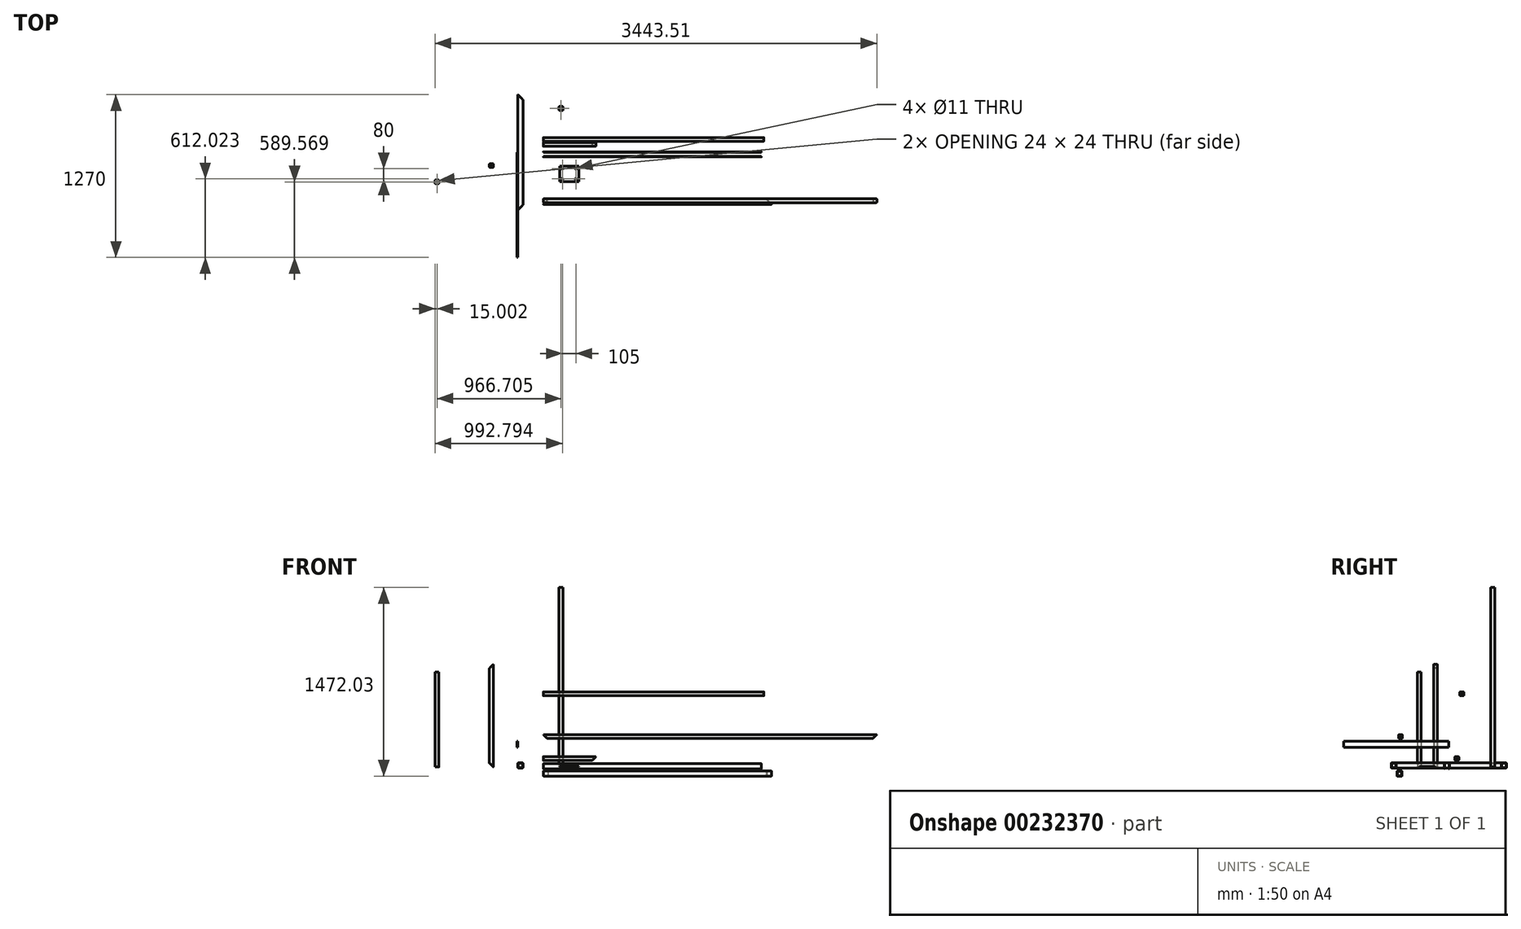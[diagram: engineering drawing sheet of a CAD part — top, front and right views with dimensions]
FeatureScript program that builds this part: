
annotation { "Feature Type Name" : "Feature", "Feature Type Description" : "" }
export const myFeature = defineFeature(function(context is Context, id is Id, definition is map)
    precondition{}
    {
        {
            var Q0;
            Q0=qCreatedBy(makeId("Right.planeOp"),FACE);
            var sketch = newSketch(context, id + "F0", { "sketchPlane" : qUnion([Q0])});
            skLineSegment(sketch, "E0.bottom", {"start": v(-31.14, 25.42) * mm, "end": v(-1.14, 25.42) * mm});
            skLineSegment(sketch, "E0.top", {"start": v(-31.14, -14.58) * mm, "end": v(-1.14, -14.58) * mm});
            skLineSegment(sketch, "E0.left", {"start": v(-36.14, 20.42) * mm, "end": v(-36.14, -9.58) * mm});
            skLineSegment(sketch, "E0.right", {"start": v(3.86, 20.42) * mm, "end": v(3.86, -9.58) * mm});
            skLineSegment(sketch, "E1.bottom", {"start": v(-31.14, 22.42) * mm, "end": v(-1.14, 22.42) * mm});
            skLineSegment(sketch, "E1.top", {"start": v(-31.14, -11.58) * mm, "end": v(-1.14, -11.58) * mm});
            skLineSegment(sketch, "E1.left", {"start": v(-33.14, 20.42) * mm, "end": v(-33.14, -9.58) * mm});
            skLineSegment(sketch, "E1.right", {"start": v(0.86, 20.42) * mm, "end": v(0.86, -9.58) * mm});
            skPoint(sketch, "E2.visualSharp", {"position": v(-36.14, 25.42) * mm});
            skArc(sketch, "E2.filletArc", {"start": v(-31.14, 25.42) * mm, "mid": v(-34.68, 23.96) * mm, "end": v(-36.14, 20.42) * mm});
            skPoint(sketch, "E3.visualSharp", {"position": v(3.86, 25.42) * mm});
            skArc(sketch, "E3.filletArc", {"start": v(3.86, 20.42) * mm, "mid": v(2.4, 23.96) * mm, "end": v(-1.14, 25.42) * mm});
            skPoint(sketch, "E4.visualSharp", {"position": v(3.86, -14.58) * mm});
            skArc(sketch, "E4.filletArc", {"start": v(-1.14, -14.58) * mm, "mid": v(2.4, -13.12) * mm, "end": v(3.86, -9.58) * mm});
            skPoint(sketch, "E5.visualSharp", {"position": v(-36.14, -14.58) * mm});
            skArc(sketch, "E5.filletArc", {"start": v(-36.14, -9.58) * mm, "mid": v(-34.68, -13.12) * mm, "end": v(-31.14, -14.58) * mm});
            skPoint(sketch, "E6.visualSharp", {"position": v(-33.14, 22.42) * mm});
            skArc(sketch, "E6.filletArc", {"start": v(-31.14, 22.42) * mm, "mid": v(-32.55, 21.83) * mm, "end": v(-33.14, 20.42) * mm});
            skPoint(sketch, "E7.visualSharp", {"position": v(0.86, 22.42) * mm});
            skArc(sketch, "E7.filletArc", {"start": v(0.86, 20.42) * mm, "mid": v(0.27, 21.83) * mm, "end": v(-1.14, 22.42) * mm});
            skPoint(sketch, "E8.visualSharp", {"position": v(0.86, -11.58) * mm});
            skArc(sketch, "E8.filletArc", {"start": v(-1.14, -11.58) * mm, "mid": v(0.27, -11) * mm, "end": v(0.86, -9.58) * mm});
            skPoint(sketch, "E9.visualSharp", {"position": v(-33.14, -11.58) * mm});
            skArc(sketch, "E9.filletArc", {"start": v(-33.14, -9.58) * mm, "mid": v(-32.55, -11) * mm, "end": v(-31.14, -11.58) * mm});
            skSolve(sketch);
        }
        {
            var Q0;
            Q0 = qSketchRegion(id + "F0", true);
            extrude(context, id + "F1", {"entities" : qUnion([Q0]), "depth" : 1700 * mm});
        }
        {
            var Q0;
            Q0=qCreatedBy(makeId("Front.planeOp"),FACE);
            var sketch = newSketch(context, id + "F2", { "sketchPlane" : qUnion([Q0])});
            skLineSegment(sketch, "E10.bottom", {"start": v(-193.38, 31.66) * mm, "end": v(-163.38, 31.66) * mm});
            skLineSegment(sketch, "E10.top", {"start": v(-193.38, -8.34) * mm, "end": v(-163.38, -8.34) * mm});
            skLineSegment(sketch, "E10.left", {"start": v(-198.38, 26.66) * mm, "end": v(-198.38, -3.34) * mm});
            skLineSegment(sketch, "E10.right", {"start": v(-158.38, 26.66) * mm, "end": v(-158.38, -3.34) * mm});
            skLineSegment(sketch, "E11.bottom", {"start": v(-193.38, 28.66) * mm, "end": v(-163.38, 28.66) * mm});
            skLineSegment(sketch, "E11.top", {"start": v(-193.38, -5.34) * mm, "end": v(-163.38, -5.34) * mm});
            skLineSegment(sketch, "E11.left", {"start": v(-195.38, 26.66) * mm, "end": v(-195.38, -3.34) * mm});
            skLineSegment(sketch, "E11.right", {"start": v(-161.38, 26.66) * mm, "end": v(-161.38, -3.34) * mm});
            skPoint(sketch, "E12.visualSharp", {"position": v(-198.38, 31.66) * mm});
            skArc(sketch, "E12.filletArc", {"start": v(-193.38, 31.66) * mm, "mid": v(-196.91, 30.2) * mm, "end": v(-198.38, 26.66) * mm});
            skPoint(sketch, "E13.visualSharp", {"position": v(-158.38, 31.66) * mm});
            skArc(sketch, "E13.filletArc", {"start": v(-158.38, 26.66) * mm, "mid": v(-159.84, 30.2) * mm, "end": v(-163.38, 31.66) * mm});
            skPoint(sketch, "E14.visualSharp", {"position": v(-158.38, -8.34) * mm});
            skArc(sketch, "E14.filletArc", {"start": v(-163.38, -8.34) * mm, "mid": v(-159.84, -6.88) * mm, "end": v(-158.38, -3.34) * mm});
            skPoint(sketch, "E15.visualSharp", {"position": v(-198.38, -8.34) * mm});
            skArc(sketch, "E15.filletArc", {"start": v(-198.38, -3.34) * mm, "mid": v(-196.91, -6.88) * mm, "end": v(-193.38, -8.34) * mm});
            skPoint(sketch, "E16.visualSharp", {"position": v(-195.38, 28.66) * mm});
            skArc(sketch, "E16.filletArc", {"start": v(-193.38, 28.66) * mm, "mid": v(-194.8, 28.07) * mm, "end": v(-195.38, 26.66) * mm});
            skPoint(sketch, "E17.visualSharp", {"position": v(-161.38, 28.66) * mm});
            skArc(sketch, "E17.filletArc", {"start": v(-161.38, 26.66) * mm, "mid": v(-161.96, 28.07) * mm, "end": v(-163.38, 28.66) * mm});
            skPoint(sketch, "E18.visualSharp", {"position": v(-161.38, -5.34) * mm});
            skArc(sketch, "E18.filletArc", {"start": v(-163.38, -5.34) * mm, "mid": v(-161.96, -4.75) * mm, "end": v(-161.38, -3.34) * mm});
            skPoint(sketch, "E19.visualSharp", {"position": v(-195.38, -5.34) * mm});
            skArc(sketch, "E19.filletArc", {"start": v(-195.38, -3.34) * mm, "mid": v(-194.8, -4.75) * mm, "end": v(-193.38, -5.34) * mm});
            skSolve(sketch);
        }
        {
            var Q0;
            Q0 = qSketchRegion(id + "F2", true);
            extrude(context, id + "F3", {"entities" : qUnion([Q0]), "depth" : 900 * mm, "symmetric" : true});
        }
        {
            var Q0;
            Q0=qCreatedBy(makeId("Top.planeOp"),FACE);
            var sketch = newSketch(context, id + "F4", { "sketchPlane" : qUnion([Q0])});
            skLineSegment(sketch, "E20.bottom", {"start": v(127.2, 357.07) * mm, "end": v(149.2, 357.07) * mm});
            skLineSegment(sketch, "E20.top", {"start": v(127.2, 327.07) * mm, "end": v(149.2, 327.07) * mm});
            skLineSegment(sketch, "E20.left", {"start": v(123.2, 353.07) * mm, "end": v(123.2, 331.07) * mm});
            skLineSegment(sketch, "E20.right", {"start": v(153.2, 353.07) * mm, "end": v(153.2, 331.07) * mm});
            skLineSegment(sketch, "E21.bottom", {"start": v(127.2, 354.07) * mm, "end": v(149.2, 354.07) * mm});
            skLineSegment(sketch, "E21.top", {"start": v(127.2, 330.07) * mm, "end": v(149.2, 330.07) * mm});
            skLineSegment(sketch, "E21.left", {"start": v(126.2, 353.07) * mm, "end": v(126.2, 331.07) * mm});
            skLineSegment(sketch, "E21.right", {"start": v(150.2, 353.07) * mm, "end": v(150.2, 331.07) * mm});
            skPoint(sketch, "E22.visualSharp", {"position": v(123.2, 357.07) * mm});
            skArc(sketch, "E22.filletArc", {"start": v(127.2, 357.07) * mm, "mid": v(124.37, 355.9) * mm, "end": v(123.2, 353.07) * mm});
            skPoint(sketch, "E23.visualSharp", {"position": v(153.2, 357.07) * mm});
            skArc(sketch, "E23.filletArc", {"start": v(153.2, 353.07) * mm, "mid": v(152.03, 355.9) * mm, "end": v(149.2, 357.07) * mm});
            skPoint(sketch, "E24.visualSharp", {"position": v(153.2, 327.07) * mm});
            skArc(sketch, "E24.filletArc", {"start": v(149.2, 327.07) * mm, "mid": v(152.03, 328.24) * mm, "end": v(153.2, 331.07) * mm});
            skPoint(sketch, "E25.visualSharp", {"position": v(123.2, 327.07) * mm});
            skArc(sketch, "E25.filletArc", {"start": v(123.2, 331.07) * mm, "mid": v(124.37, 328.24) * mm, "end": v(127.2, 327.07) * mm});
            skPoint(sketch, "E26.visualSharp", {"position": v(126.2, 354.07) * mm});
            skArc(sketch, "E26.filletArc", {"start": v(127.2, 354.07) * mm, "mid": v(126.5, 353.77) * mm, "end": v(126.2, 353.07) * mm});
            skPoint(sketch, "E27.visualSharp", {"position": v(150.2, 354.07) * mm});
            skArc(sketch, "E27.filletArc", {"start": v(150.2, 353.07) * mm, "mid": v(149.9, 353.77) * mm, "end": v(149.2, 354.07) * mm});
            skPoint(sketch, "E28.visualSharp", {"position": v(150.2, 330.07) * mm});
            skArc(sketch, "E28.filletArc", {"start": v(149.2, 330.07) * mm, "mid": v(149.9, 330.36) * mm, "end": v(150.2, 331.07) * mm});
            skPoint(sketch, "E29.visualSharp", {"position": v(126.2, 330.07) * mm});
            skArc(sketch, "E29.filletArc", {"start": v(126.2, 331.07) * mm, "mid": v(126.5, 330.36) * mm, "end": v(127.2, 330.07) * mm});
            skSolve(sketch);
        }
        {
            var Q0;
            Q0 = qSketchRegion(id + "F4", true);
            extrude(context, id + "F5", {"entities" : qUnion([Q0]), "depth" : 1400 * mm});
        }
        {
            var Q0;
            Q0=qCreatedBy(makeId("Right.planeOp"),FACE);
            var sketch = newSketch(context, id + "F6", { "sketchPlane" : qUnion([Q0])});
            skLineSegment(sketch, "E30.bottom", {"start": v(89.68, 585.85) * mm, "end": v(111.68, 585.85) * mm});
            skLineSegment(sketch, "E30.top", {"start": v(89.68, 555.85) * mm, "end": v(111.68, 555.85) * mm});
            skLineSegment(sketch, "E30.left", {"start": v(85.68, 581.85) * mm, "end": v(85.68, 559.85) * mm});
            skLineSegment(sketch, "E30.right", {"start": v(115.68, 581.85) * mm, "end": v(115.68, 559.85) * mm});
            skLineSegment(sketch, "E31.bottom", {"start": v(89.68, 582.85) * mm, "end": v(111.68, 582.85) * mm});
            skLineSegment(sketch, "E31.top", {"start": v(89.68, 558.85) * mm, "end": v(111.68, 558.85) * mm});
            skLineSegment(sketch, "E31.left", {"start": v(88.68, 581.85) * mm, "end": v(88.68, 559.85) * mm});
            skLineSegment(sketch, "E31.right", {"start": v(112.68, 581.85) * mm, "end": v(112.68, 559.85) * mm});
            skPoint(sketch, "E32.visualSharp", {"position": v(85.68, 585.85) * mm});
            skArc(sketch, "E32.filletArc", {"start": v(89.68, 585.85) * mm, "mid": v(86.85, 584.67) * mm, "end": v(85.68, 581.85) * mm});
            skPoint(sketch, "E33.visualSharp", {"position": v(115.68, 585.85) * mm});
            skArc(sketch, "E33.filletArc", {"start": v(115.68, 581.85) * mm, "mid": v(114.5, 584.67) * mm, "end": v(111.68, 585.85) * mm});
            skPoint(sketch, "E34.visualSharp", {"position": v(115.68, 555.85) * mm});
            skArc(sketch, "E34.filletArc", {"start": v(111.68, 555.85) * mm, "mid": v(114.5, 557.02) * mm, "end": v(115.68, 559.85) * mm});
            skPoint(sketch, "E35.visualSharp", {"position": v(85.68, 555.85) * mm});
            skArc(sketch, "E35.filletArc", {"start": v(85.68, 559.85) * mm, "mid": v(86.85, 557.02) * mm, "end": v(89.68, 555.85) * mm});
            skPoint(sketch, "E36.visualSharp", {"position": v(88.68, 582.85) * mm});
            skArc(sketch, "E36.filletArc", {"start": v(89.68, 582.85) * mm, "mid": v(88.97, 582.55) * mm, "end": v(88.68, 581.85) * mm});
            skPoint(sketch, "E37.visualSharp", {"position": v(112.68, 582.85) * mm});
            skArc(sketch, "E37.filletArc", {"start": v(112.68, 581.85) * mm, "mid": v(112.39, 582.55) * mm, "end": v(111.68, 582.85) * mm});
            skPoint(sketch, "E38.visualSharp", {"position": v(112.68, 558.85) * mm});
            skArc(sketch, "E38.filletArc", {"start": v(111.68, 558.85) * mm, "mid": v(112.39, 559.14) * mm, "end": v(112.68, 559.85) * mm});
            skPoint(sketch, "E39.visualSharp", {"position": v(88.68, 558.85) * mm});
            skArc(sketch, "E39.filletArc", {"start": v(88.68, 559.85) * mm, "mid": v(88.97, 559.14) * mm, "end": v(89.68, 558.85) * mm});
            skSolve(sketch);
        }
        {
            var Q0;
            Q0 = qSketchRegion(id + "F6", true);
            extrude(context, id + "F7", {"entities" : qUnion([Q0]), "depth" : 1720 * mm});
        }
        {
            var Q0;
            Q0=qCreatedBy(makeId("Top.planeOp"),FACE);
            var sketch = newSketch(context, id + "F8", { "sketchPlane" : qUnion([Q0])});
            skLineSegment(sketch, "E40.bottom", {"start": v(276.78, -107.98) * mm, "end": v(126.78, -107.98) * mm});
            skLineSegment(sketch, "E40.top", {"start": v(276.78, -227.98) * mm, "end": v(126.78, -227.98) * mm});
            skLineSegment(sketch, "E40.left", {"start": v(276.78, -107.98) * mm, "end": v(276.78, -227.98) * mm});
            skLineSegment(sketch, "E40.right", {"start": v(126.78, -107.98) * mm, "end": v(126.78, -227.98) * mm});
            skPoint(sketch, "E40.middle", {"position": v(201.78, -167.98) * mm});
            skLineSegment(sketch, "E41", {"start": v(126.78, -107.98) * mm, "end": v(276.78, -227.98) * mm, "construction": true});
            skLineSegment(sketch, "E42.bottom", {"start": v(254.28, -127.98) * mm, "end": v(149.28, -127.98) * mm, "construction": true});
            skLineSegment(sketch, "E42.top", {"start": v(254.28, -207.98) * mm, "end": v(149.28, -207.98) * mm, "construction": true});
            skLineSegment(sketch, "E42.left", {"start": v(254.28, -127.98) * mm, "end": v(254.28, -207.98) * mm, "construction": true});
            skLineSegment(sketch, "E42.right", {"start": v(149.28, -127.98) * mm, "end": v(149.28, -207.98) * mm, "construction": true});
            skCircle(sketch, "E43", {"center": v(149.28, -207.98) * mm, "radius": 5.5 * mm});
            skCircle(sketch, "E44", {"center": v(254.28, -127.98) * mm, "radius": 5.5 * mm});
            skCircle(sketch, "E45", {"center": v(149.28, -127.98) * mm, "radius": 5.5 * mm});
            skCircle(sketch, "E46", {"center": v(254.28, -207.98) * mm, "radius": 5.5 * mm});
            skLineSegment(sketch, "E47", {"start": v(254.28, -127.98) * mm, "end": v(149.28, -207.98) * mm, "construction": true});
            skSolve(sketch);
        }
        {
            var Q0;
            Q0 = qSketchRegion(id + "F8", true);
            extrude(context, id + "F9", {"entities" : qUnion([Q0]), "depth" : 5 * mm});
        }
        {
            var Q0;
            Q0=qCreatedBy(makeId("Right.planeOp"),FACE);
            var sketch = newSketch(context, id + "F10", { "sketchPlane" : qUnion([Q0])});
            skLineSegment(sketch, "E48.bottom", {"start": v(-388.3, 252.81) * mm, "end": v(-366.3, 252.81) * mm});
            skLineSegment(sketch, "E48.top", {"start": v(-388.3, 222.81) * mm, "end": v(-366.3, 222.81) * mm});
            skLineSegment(sketch, "E48.left", {"start": v(-392.3, 248.81) * mm, "end": v(-392.3, 226.81) * mm});
            skLineSegment(sketch, "E48.right", {"start": v(-362.3, 248.81) * mm, "end": v(-362.3, 226.81) * mm});
            skLineSegment(sketch, "E49.bottom", {"start": v(-388.3, 249.81) * mm, "end": v(-366.3, 249.81) * mm});
            skLineSegment(sketch, "E49.top", {"start": v(-388.3, 225.81) * mm, "end": v(-366.3, 225.81) * mm});
            skLineSegment(sketch, "E49.left", {"start": v(-389.3, 248.81) * mm, "end": v(-389.3, 226.81) * mm});
            skLineSegment(sketch, "E49.right", {"start": v(-365.3, 248.81) * mm, "end": v(-365.3, 226.81) * mm});
            skPoint(sketch, "E50.visualSharp", {"position": v(-392.3, 252.81) * mm});
            skArc(sketch, "E50.filletArc", {"start": v(-388.3, 252.81) * mm, "mid": v(-391.13, 251.64) * mm, "end": v(-392.3, 248.81) * mm});
            skPoint(sketch, "E51.visualSharp", {"position": v(-362.3, 252.81) * mm});
            skArc(sketch, "E51.filletArc", {"start": v(-362.3, 248.81) * mm, "mid": v(-363.47, 251.64) * mm, "end": v(-366.3, 252.81) * mm});
            skPoint(sketch, "E52.visualSharp", {"position": v(-362.3, 222.81) * mm});
            skArc(sketch, "E52.filletArc", {"start": v(-366.3, 222.81) * mm, "mid": v(-363.47, 223.98) * mm, "end": v(-362.3, 226.81) * mm});
            skPoint(sketch, "E53.visualSharp", {"position": v(-392.3, 222.81) * mm});
            skArc(sketch, "E53.filletArc", {"start": v(-392.3, 226.81) * mm, "mid": v(-391.13, 223.98) * mm, "end": v(-388.3, 222.81) * mm});
            skPoint(sketch, "E54.visualSharp", {"position": v(-389.3, 249.81) * mm});
            skArc(sketch, "E54.filletArc", {"start": v(-388.3, 249.81) * mm, "mid": v(-389, 249.52) * mm, "end": v(-389.3, 248.81) * mm});
            skPoint(sketch, "E55.visualSharp", {"position": v(-365.3, 249.81) * mm});
            skArc(sketch, "E55.filletArc", {"start": v(-365.3, 248.81) * mm, "mid": v(-365.6, 249.52) * mm, "end": v(-366.3, 249.81) * mm});
            skPoint(sketch, "E56.visualSharp", {"position": v(-365.3, 225.81) * mm});
            skArc(sketch, "E56.filletArc", {"start": v(-366.3, 225.81) * mm, "mid": v(-365.6, 226.1) * mm, "end": v(-365.3, 226.81) * mm});
            skPoint(sketch, "E57.visualSharp", {"position": v(-389.3, 225.81) * mm});
            skArc(sketch, "E57.filletArc", {"start": v(-389.3, 226.81) * mm, "mid": v(-389, 226.1) * mm, "end": v(-388.3, 225.81) * mm});
            skSolve(sketch);
        }
        {
            var Q0;
            Q0 = qSketchRegion(id + "F10", true);
            extrude(context, id + "F11", {"entities" : qUnion([Q0]), "depth" : 2600 * mm});
        }
        {
            var Q0;
            Q0=qCreatedBy(makeId("Top.planeOp"),FACE);
            var sketch = newSketch(context, id + "F12", { "sketchPlane" : qUnion([Q0])});
            skLineSegment(sketch, "E58.bottom", {"start": v(-415.78, -88.88) * mm, "end": v(-393.78, -88.88) * mm});
            skLineSegment(sketch, "E58.top", {"start": v(-415.78, -118.88) * mm, "end": v(-393.78, -118.88) * mm});
            skLineSegment(sketch, "E58.left", {"start": v(-419.78, -92.88) * mm, "end": v(-419.78, -114.88) * mm});
            skLineSegment(sketch, "E58.right", {"start": v(-389.78, -92.88) * mm, "end": v(-389.78, -114.88) * mm});
            skLineSegment(sketch, "E59.bottom", {"start": v(-415.78, -91.88) * mm, "end": v(-393.78, -91.88) * mm});
            skLineSegment(sketch, "E59.top", {"start": v(-415.78, -115.88) * mm, "end": v(-393.78, -115.88) * mm});
            skLineSegment(sketch, "E59.left", {"start": v(-416.78, -92.88) * mm, "end": v(-416.78, -114.88) * mm});
            skLineSegment(sketch, "E59.right", {"start": v(-392.78, -92.88) * mm, "end": v(-392.78, -114.88) * mm});
            skPoint(sketch, "E60.visualSharp", {"position": v(-419.78, -88.88) * mm});
            skArc(sketch, "E60.filletArc", {"start": v(-415.78, -88.88) * mm, "mid": v(-418.6, -90.05) * mm, "end": v(-419.78, -92.88) * mm});
            skPoint(sketch, "E61.visualSharp", {"position": v(-389.78, -88.88) * mm});
            skArc(sketch, "E61.filletArc", {"start": v(-389.78, -92.88) * mm, "mid": v(-390.95, -90.05) * mm, "end": v(-393.78, -88.88) * mm});
            skPoint(sketch, "E62.visualSharp", {"position": v(-389.78, -118.88) * mm});
            skArc(sketch, "E62.filletArc", {"start": v(-393.78, -118.88) * mm, "mid": v(-390.95, -117.71) * mm, "end": v(-389.78, -114.88) * mm});
            skPoint(sketch, "E63.visualSharp", {"position": v(-419.78, -118.88) * mm});
            skArc(sketch, "E63.filletArc", {"start": v(-419.78, -114.88) * mm, "mid": v(-418.6, -117.71) * mm, "end": v(-415.78, -118.88) * mm});
            skPoint(sketch, "E64.visualSharp", {"position": v(-416.78, -91.88) * mm});
            skArc(sketch, "E64.filletArc", {"start": v(-415.78, -91.88) * mm, "mid": v(-416.49, -92.17) * mm, "end": v(-416.78, -92.88) * mm});
            skPoint(sketch, "E65.visualSharp", {"position": v(-392.78, -91.88) * mm});
            skArc(sketch, "E65.filletArc", {"start": v(-392.78, -92.88) * mm, "mid": v(-393.07, -92.17) * mm, "end": v(-393.78, -91.88) * mm});
            skPoint(sketch, "E66.visualSharp", {"position": v(-392.78, -115.88) * mm});
            skArc(sketch, "E66.filletArc", {"start": v(-393.78, -115.88) * mm, "mid": v(-393.07, -115.59) * mm, "end": v(-392.78, -114.88) * mm});
            skPoint(sketch, "E67.visualSharp", {"position": v(-416.78, -115.88) * mm});
            skArc(sketch, "E67.filletArc", {"start": v(-416.78, -114.88) * mm, "mid": v(-416.49, -115.59) * mm, "end": v(-415.78, -115.88) * mm});
            skSolve(sketch);
        }
        {
            var Q0;
            Q0 = qSketchRegion(id + "F12", true);
            extrude(context, id + "F13", {"entities" : qUnion([Q0]), "depth" : 800 * mm});
        }
        {
            var Q0;
            Q0=qCreatedBy(makeId("Right.planeOp"),FACE);
            var sketch = newSketch(context, id + "F14", { "sketchPlane" : qUnion([Q0])});
            skLineSegment(sketch, "E68.bottom", {"start": v(50.9, 81.17) * mm, "end": v(72.9, 81.17) * mm});
            skLineSegment(sketch, "E68.top", {"start": v(50.9, 51.17) * mm, "end": v(72.9, 51.17) * mm});
            skLineSegment(sketch, "E68.left", {"start": v(46.9, 77.17) * mm, "end": v(46.9, 55.17) * mm});
            skLineSegment(sketch, "E68.right", {"start": v(76.9, 77.17) * mm, "end": v(76.9, 55.17) * mm});
            skLineSegment(sketch, "E69.bottom", {"start": v(50.9, 78.17) * mm, "end": v(72.9, 78.17) * mm});
            skLineSegment(sketch, "E69.top", {"start": v(50.9, 54.17) * mm, "end": v(72.9, 54.17) * mm});
            skLineSegment(sketch, "E69.left", {"start": v(49.9, 77.17) * mm, "end": v(49.9, 55.17) * mm});
            skLineSegment(sketch, "E69.right", {"start": v(73.9, 77.17) * mm, "end": v(73.9, 55.17) * mm});
            skPoint(sketch, "E70.visualSharp", {"position": v(46.9, 81.17) * mm});
            skArc(sketch, "E70.filletArc", {"start": v(50.9, 81.17) * mm, "mid": v(48.07, 80) * mm, "end": v(46.9, 77.17) * mm});
            skPoint(sketch, "E71.visualSharp", {"position": v(76.9, 81.17) * mm});
            skArc(sketch, "E71.filletArc", {"start": v(76.9, 77.17) * mm, "mid": v(75.73, 80) * mm, "end": v(72.9, 81.17) * mm});
            skPoint(sketch, "E72.visualSharp", {"position": v(76.9, 51.17) * mm});
            skArc(sketch, "E72.filletArc", {"start": v(72.9, 51.17) * mm, "mid": v(75.73, 52.34) * mm, "end": v(76.9, 55.17) * mm});
            skPoint(sketch, "E73.visualSharp", {"position": v(46.9, 51.17) * mm});
            skArc(sketch, "E73.filletArc", {"start": v(46.9, 55.17) * mm, "mid": v(48.07, 52.34) * mm, "end": v(50.9, 51.17) * mm});
            skPoint(sketch, "E74.visualSharp", {"position": v(49.9, 78.17) * mm});
            skArc(sketch, "E74.filletArc", {"start": v(50.9, 78.17) * mm, "mid": v(50.2, 77.88) * mm, "end": v(49.9, 77.17) * mm});
            skPoint(sketch, "E75.visualSharp", {"position": v(73.9, 78.17) * mm});
            skArc(sketch, "E75.filletArc", {"start": v(73.9, 77.17) * mm, "mid": v(73.6, 77.88) * mm, "end": v(72.9, 78.17) * mm});
            skPoint(sketch, "E76.visualSharp", {"position": v(73.9, 54.17) * mm});
            skArc(sketch, "E76.filletArc", {"start": v(72.9, 54.17) * mm, "mid": v(73.6, 54.46) * mm, "end": v(73.9, 55.17) * mm});
            skPoint(sketch, "E77.visualSharp", {"position": v(49.9, 54.17) * mm});
            skArc(sketch, "E77.filletArc", {"start": v(49.9, 55.17) * mm, "mid": v(50.2, 54.46) * mm, "end": v(50.9, 54.17) * mm});
            skSolve(sketch);
        }
        {
            var Q0;
            Q0 = qSketchRegion(id + "F14", true);
            extrude(context, id + "F15", {"entities" : qUnion([Q0]), "depth" : 410 * mm});
        }
        {
            var Q0;
            Q0=qCreatedBy(makeId("Top.planeOp"),FACE);
            var sketch = newSketch(context, id + "F16", { "sketchPlane" : qUnion([Q0])});
            skLineSegment(sketch, "E78.bottom", {"start": v(-839.5, -215.43) * mm, "end": v(-817.5, -215.43) * mm});
            skLineSegment(sketch, "E78.top", {"start": v(-839.5, -245.43) * mm, "end": v(-817.5, -245.43) * mm});
            skLineSegment(sketch, "E78.left", {"start": v(-843.5, -219.43) * mm, "end": v(-843.5, -241.43) * mm});
            skLineSegment(sketch, "E78.right", {"start": v(-813.5, -219.43) * mm, "end": v(-813.5, -241.43) * mm});
            skLineSegment(sketch, "E79.bottom", {"start": v(-839.5, -218.43) * mm, "end": v(-817.5, -218.43) * mm});
            skLineSegment(sketch, "E79.top", {"start": v(-839.5, -242.43) * mm, "end": v(-817.5, -242.43) * mm});
            skLineSegment(sketch, "E79.left", {"start": v(-840.5, -219.43) * mm, "end": v(-840.5, -241.43) * mm});
            skLineSegment(sketch, "E79.right", {"start": v(-816.5, -219.43) * mm, "end": v(-816.5, -241.43) * mm});
            skPoint(sketch, "E80.visualSharp", {"position": v(-843.5, -215.43) * mm});
            skArc(sketch, "E80.filletArc", {"start": v(-839.5, -215.43) * mm, "mid": v(-842.34, -216.6) * mm, "end": v(-843.5, -219.43) * mm});
            skPoint(sketch, "E81.visualSharp", {"position": v(-813.5, -215.43) * mm});
            skArc(sketch, "E81.filletArc", {"start": v(-813.5, -219.43) * mm, "mid": v(-814.68, -216.6) * mm, "end": v(-817.5, -215.43) * mm});
            skPoint(sketch, "E82.visualSharp", {"position": v(-813.5, -245.43) * mm});
            skArc(sketch, "E82.filletArc", {"start": v(-817.5, -245.43) * mm, "mid": v(-814.68, -244.26) * mm, "end": v(-813.5, -241.43) * mm});
            skPoint(sketch, "E83.visualSharp", {"position": v(-843.5, -245.43) * mm});
            skArc(sketch, "E83.filletArc", {"start": v(-843.5, -241.43) * mm, "mid": v(-842.34, -244.26) * mm, "end": v(-839.5, -245.43) * mm});
            skPoint(sketch, "E84.visualSharp", {"position": v(-840.5, -218.43) * mm});
            skArc(sketch, "E84.filletArc", {"start": v(-839.5, -218.43) * mm, "mid": v(-840.22, -218.72) * mm, "end": v(-840.5, -219.43) * mm});
            skPoint(sketch, "E85.visualSharp", {"position": v(-816.5, -218.43) * mm});
            skArc(sketch, "E85.filletArc", {"start": v(-816.5, -219.43) * mm, "mid": v(-816.8, -218.72) * mm, "end": v(-817.5, -218.43) * mm});
            skPoint(sketch, "E86.visualSharp", {"position": v(-816.5, -242.43) * mm});
            skArc(sketch, "E86.filletArc", {"start": v(-817.5, -242.43) * mm, "mid": v(-816.8, -242.14) * mm, "end": v(-816.5, -241.43) * mm});
            skPoint(sketch, "E87.visualSharp", {"position": v(-840.5, -242.43) * mm});
            skArc(sketch, "E87.filletArc", {"start": v(-840.5, -241.43) * mm, "mid": v(-840.22, -242.14) * mm, "end": v(-839.5, -242.43) * mm});
            skSolve(sketch);
        }
        {
            var Q0;
            Q0 = qSketchRegion(id + "F16", true);
            extrude(context, id + "F17", {"entities" : qUnion([Q0]), "depth" : 740 * mm});
        }
        {
            var Q0;
            Q0=makeQuery(id+"F11.opExtrude","SWEPT_FACE",FACE,{"disambiguationData":[OSD([sQuery(id+"F10.wireOp",EDGE,"E48.left")])]});
            var sketch = newSketch(context, id + "F18", { "sketchPlane" : qUnion([Q0])});
            skPoint(sketch, "E88.0", {"position": v(2600, 252.81) * mm});
            skPoint(sketch, "E89.0", {"position": v(2600, 222.81) * mm});
            skLineSegment(sketch, "E90.0", {"start": v(2600, 222.81) * mm, "end": v(2570, 222.81) * mm});
            skLineSegment(sketch, "E91", {"start": v(2600, 252.81) * mm, "end": v(2600, 222.81) * mm});
            skLineSegment(sketch, "E92", {"start": v(2600, 252.81) * mm, "end": v(2570, 222.81) * mm});
            skPoint(sketch, "E93.0", {"position": v(0, 252.81) * mm});
            skLineSegment(sketch, "E94", {"start": v(0, 222.81) * mm, "end": v(0, 252.81) * mm});
            skLineSegment(sketch, "E95", {"start": v(0, 252.81) * mm, "end": v(30, 222.81) * mm});
            skLineSegment(sketch, "E96.trimOffspring", {"start": v(30, 222.81) * mm, "end": v(0, 222.81) * mm});
            skSolve(sketch);
        }
        {
            var Q0;
            Q0 = qSketchRegion(id + "F18", true);
            extrude(context, id + "F19", {"entities" : qUnion([Q0]), "operationType" : NewBodyOperationType.REMOVE, "endBound" : BoundingType.THROUGH_ALL, "oppositeDirection" : true, "depth" : 25 * mm});
        }
        {
            var Q0;
            Q0=makeQuery(id+"F13.opExtrude","SWEPT_FACE",FACE,{"disambiguationData":[OSD([sQuery(id+"F12.wireOp",EDGE,"E58.top")])]});
            var sketch = newSketch(context, id + "F20", { "sketchPlane" : qUnion([Q0])});
            skPoint(sketch, "E97.0", {"position": v(-389.78, 800) * mm});
            skPoint(sketch, "E98.0", {"position": v(-419.78, 800) * mm});
            skLineSegment(sketch, "E99.0", {"start": v(-419.78, 800) * mm, "end": v(-419.78, 770) * mm});
            skPoint(sketch, "E100.0", {"position": v(-389.78, 0) * mm});
            skLineSegment(sketch, "E101", {"start": v(-419.78, 0) * mm, "end": v(-389.78, 0) * mm});
            skLineSegment(sketch, "E102", {"start": v(-389.78, 0) * mm, "end": v(-419.78, 30) * mm});
            skLineSegment(sketch, "E103", {"start": v(-419.78, 800) * mm, "end": v(-389.78, 800) * mm});
            skLineSegment(sketch, "E104", {"start": v(-389.78, 800) * mm, "end": v(-419.78, 770) * mm});
            skLineSegment(sketch, "E105.trimOffspring", {"start": v(-419.78, 30) * mm, "end": v(-419.78, 0) * mm});
            skSolve(sketch);
        }
        {
            var Q0;
            Q0 = qSketchRegion(id + "F20", true);
            extrude(context, id + "F21", {"entities" : qUnion([Q0]), "operationType" : NewBodyOperationType.REMOVE, "endBound" : BoundingType.THROUGH_ALL, "oppositeDirection" : true, "depth" : 25 * mm});
        }
        {
            var Q0;
            Q0=makeQuery(id+"F15.opExtrude","SWEPT_FACE",FACE,{"disambiguationData":[OSD([sQuery(id+"F14.wireOp",EDGE,"E68.left")])]});
            var sketch = newSketch(context, id + "F22", { "sketchPlane" : qUnion([Q0])});
            skPoint(sketch, "E106.0", {"position": v(410, 81.17) * mm});
            skPoint(sketch, "E107.0", {"position": v(410, 51.17) * mm});
            skLineSegment(sketch, "E108.0", {"start": v(410, 51.17) * mm, "end": v(380, 51.17) * mm});
            skLineSegment(sketch, "E109", {"start": v(410, 51.17) * mm, "end": v(410, 81.17) * mm});
            skLineSegment(sketch, "E110", {"start": v(410, 81.17) * mm, "end": v(380, 51.17) * mm});
            skPoint(sketch, "E111.orphan", {"position": v(0, 51.17) * mm});
            skSolve(sketch);
        }
        {
            var Q0;
            Q0 = qSketchRegion(id + "F22", true);
            extrude(context, id + "F23", {"entities" : qUnion([Q0]), "operationType" : NewBodyOperationType.REMOVE, "endBound" : BoundingType.THROUGH_ALL, "oppositeDirection" : true, "depth" : 25 * mm});
        }
        {
            var Q0;
            Q0=qCreatedBy(makeId("Right.planeOp"),FACE);
            var sketch = newSketch(context, id + "F24", { "sketchPlane" : qUnion([Q0])});
            skLineSegment(sketch, "E112.bottom", {"start": v(-400.04, -32.03) * mm, "end": v(-370.04, -32.03) * mm});
            skLineSegment(sketch, "E112.top", {"start": v(-400.04, -72.03) * mm, "end": v(-370.04, -72.03) * mm});
            skLineSegment(sketch, "E112.left", {"start": v(-405.04, -37.03) * mm, "end": v(-405.04, -67.03) * mm});
            skLineSegment(sketch, "E112.right", {"start": v(-365.04, -37.03) * mm, "end": v(-365.04, -67.03) * mm});
            skLineSegment(sketch, "E113.bottom", {"start": v(-400.04, -35.03) * mm, "end": v(-370.04, -35.03) * mm});
            skLineSegment(sketch, "E113.top", {"start": v(-400.04, -69.03) * mm, "end": v(-370.04, -69.03) * mm});
            skLineSegment(sketch, "E113.left", {"start": v(-402.04, -37.03) * mm, "end": v(-402.04, -67.03) * mm});
            skLineSegment(sketch, "E113.right", {"start": v(-368.04, -37.03) * mm, "end": v(-368.04, -67.03) * mm});
            skPoint(sketch, "E114.visualSharp", {"position": v(-405.04, -32.03) * mm});
            skArc(sketch, "E114.filletArc", {"start": v(-400.04, -32.03) * mm, "mid": v(-403.58, -33.5) * mm, "end": v(-405.04, -37.03) * mm});
            skPoint(sketch, "E115.visualSharp", {"position": v(-365.04, -32.03) * mm});
            skArc(sketch, "E115.filletArc", {"start": v(-365.04, -37.03) * mm, "mid": v(-366.5, -33.5) * mm, "end": v(-370.04, -32.03) * mm});
            skPoint(sketch, "E116.visualSharp", {"position": v(-365.04, -72.03) * mm});
            skArc(sketch, "E116.filletArc", {"start": v(-370.04, -72.03) * mm, "mid": v(-366.5, -70.56) * mm, "end": v(-365.04, -67.03) * mm});
            skPoint(sketch, "E117.visualSharp", {"position": v(-405.04, -72.03) * mm});
            skArc(sketch, "E117.filletArc", {"start": v(-405.04, -67.03) * mm, "mid": v(-403.58, -70.56) * mm, "end": v(-400.04, -72.03) * mm});
            skPoint(sketch, "E118.visualSharp", {"position": v(-402.04, -35.03) * mm});
            skArc(sketch, "E118.filletArc", {"start": v(-400.04, -35.03) * mm, "mid": v(-401.46, -35.61) * mm, "end": v(-402.04, -37.03) * mm});
            skPoint(sketch, "E119.visualSharp", {"position": v(-368.04, -35.03) * mm});
            skArc(sketch, "E119.filletArc", {"start": v(-368.04, -37.03) * mm, "mid": v(-368.63, -35.61) * mm, "end": v(-370.04, -35.03) * mm});
            skPoint(sketch, "E120.visualSharp", {"position": v(-368.04, -69.03) * mm});
            skArc(sketch, "E120.filletArc", {"start": v(-370.04, -69.03) * mm, "mid": v(-368.63, -68.44) * mm, "end": v(-368.04, -67.03) * mm});
            skPoint(sketch, "E121.visualSharp", {"position": v(-402.04, -69.03) * mm});
            skArc(sketch, "E121.filletArc", {"start": v(-402.04, -67.03) * mm, "mid": v(-401.46, -68.44) * mm, "end": v(-400.04, -69.03) * mm});
            skSolve(sketch);
        }
        {
            var Q0;
            Q0 = qSketchRegion(id + "F24", true);
            extrude(context, id + "F25", {"entities" : qUnion([Q0]), "depth" : 1780 * mm});
        }
        {
            var Q0;
            Q0=makeQuery(id+"F3.opExtrude","SWEPT_FACE",FACE,{"disambiguationData":[OSD([sQuery(id+"F2.wireOp",EDGE,"E10.bottom")])]});
            var sketch = newSketch(context, id + "F26", { "sketchPlane" : qUnion([Q0])});
            skPoint(sketch, "E122.0", {"position": v(-158.38, 450) * mm});
            skPoint(sketch, "E123.0", {"position": v(-198.38, 450) * mm});
            skLineSegment(sketch, "E124.0", {"start": v(-158.38, -450) * mm, "end": v(-158.38, -410) * mm});
            skPoint(sketch, "E125.0", {"position": v(-198.38, -450) * mm});
            skPoint(sketch, "E126.0", {"position": v(0, -405.04) * mm});
            skPoint(sketch, "E127.0", {"position": v(0, -365.04) * mm});
            skLineSegment(sketch, "E128.0", {"start": v(1780, -365.04) * mm, "end": v(1740, -365.04) * mm});
            skPoint(sketch, "E129.0", {"position": v(1780, -405.04) * mm});
            skLineSegment(sketch, "E130", {"start": v(1780, -365.04) * mm, "end": v(1780, -405.04) * mm});
            skLineSegment(sketch, "E131", {"start": v(1780, -405.04) * mm, "end": v(1740, -365.04) * mm});
            skLineSegment(sketch, "E132", {"start": v(0, -365.04) * mm, "end": v(0, -405.04) * mm});
            skLineSegment(sketch, "E133", {"start": v(0, -405.04) * mm, "end": v(40, -365.04) * mm});
            skLineSegment(sketch, "E134.trimOffspring", {"start": v(40, -365.04) * mm, "end": v(0, -365.04) * mm});
            skLineSegment(sketch, "E135", {"start": v(-158.38, -450) * mm, "end": v(-198.38, -450) * mm});
            skLineSegment(sketch, "E136", {"start": v(-198.38, -450) * mm, "end": v(-158.38, -410) * mm});
            skLineSegment(sketch, "E137", {"start": v(-158.38, 450) * mm, "end": v(-198.38, 450) * mm});
            skLineSegment(sketch, "E138", {"start": v(-198.38, 450) * mm, "end": v(-158.38, 410) * mm});
            skLineSegment(sketch, "E139.trimOffspring", {"start": v(-158.38, 410) * mm, "end": v(-158.38, 450) * mm});
            skSolve(sketch);
        }
        {
            var Q0;
            Q0 = qSketchRegion(id + "F26", true);
            var Q1;
            Q1=makeQuery(id+"F1.opExtrude","SWEPT_FACE",FACE,{"disambiguationData":[OSD([sQuery(id+"F0.wireOp",EDGE,"E0.bottom")])]});
            extrude(context, id + "F27", {"entities" : qUnion([Q0, Q1]), "operationType" : NewBodyOperationType.REMOVE, "endBound" : BoundingType.THROUGH_ALL, "oppositeDirection" : true, "depth" : 25 * mm});
        }
        {
            var Q0;
            Q0 = qSketchRegion(id + "F26", true);
            extrude(context, id + "F28", {"entities" : qUnion([Q0]), "operationType" : NewBodyOperationType.REMOVE, "endBound" : BoundingType.THROUGH_ALL, "oppositeDirection" : true, "depth" : 25 * mm});
        }
        {
            var Q0;
            Q0=qCreatedBy(makeId("Front.planeOp"),FACE);
            var sketch = newSketch(context, id + "F29", { "sketchPlane" : qUnion([Q0])});
            skLineSegment(sketch, "E140.bottom", {"start": v(-204.97, 151.48) * mm, "end": v(-198.97, 151.48) * mm});
            skLineSegment(sketch, "E140.top", {"start": v(-204.97, 201.48) * mm, "end": v(-198.97, 201.48) * mm});
            skLineSegment(sketch, "E140.left", {"start": v(-204.97, 151.48) * mm, "end": v(-204.97, 201.48) * mm});
            skLineSegment(sketch, "E140.right", {"start": v(-198.97, 151.48) * mm, "end": v(-198.97, 201.48) * mm});
            skSolve(sketch);
        }
        {
            var Q0;
            Q0=makeQuery(id+"F29.imprint","IMPRINT",FACE,{"disambiguationData":[TD([[makeQuery(id+"F29.imprint","IMPRINT",EDGE,{"derivedFrom":sQuery(id+"F29.wireOp",EDGE,"E140.bottom")}),1.0]])]});
            extrude(context, id + "F30", {"entities" : qUnion([Q0]), "depth" : 820 * mm});
        }
    });
